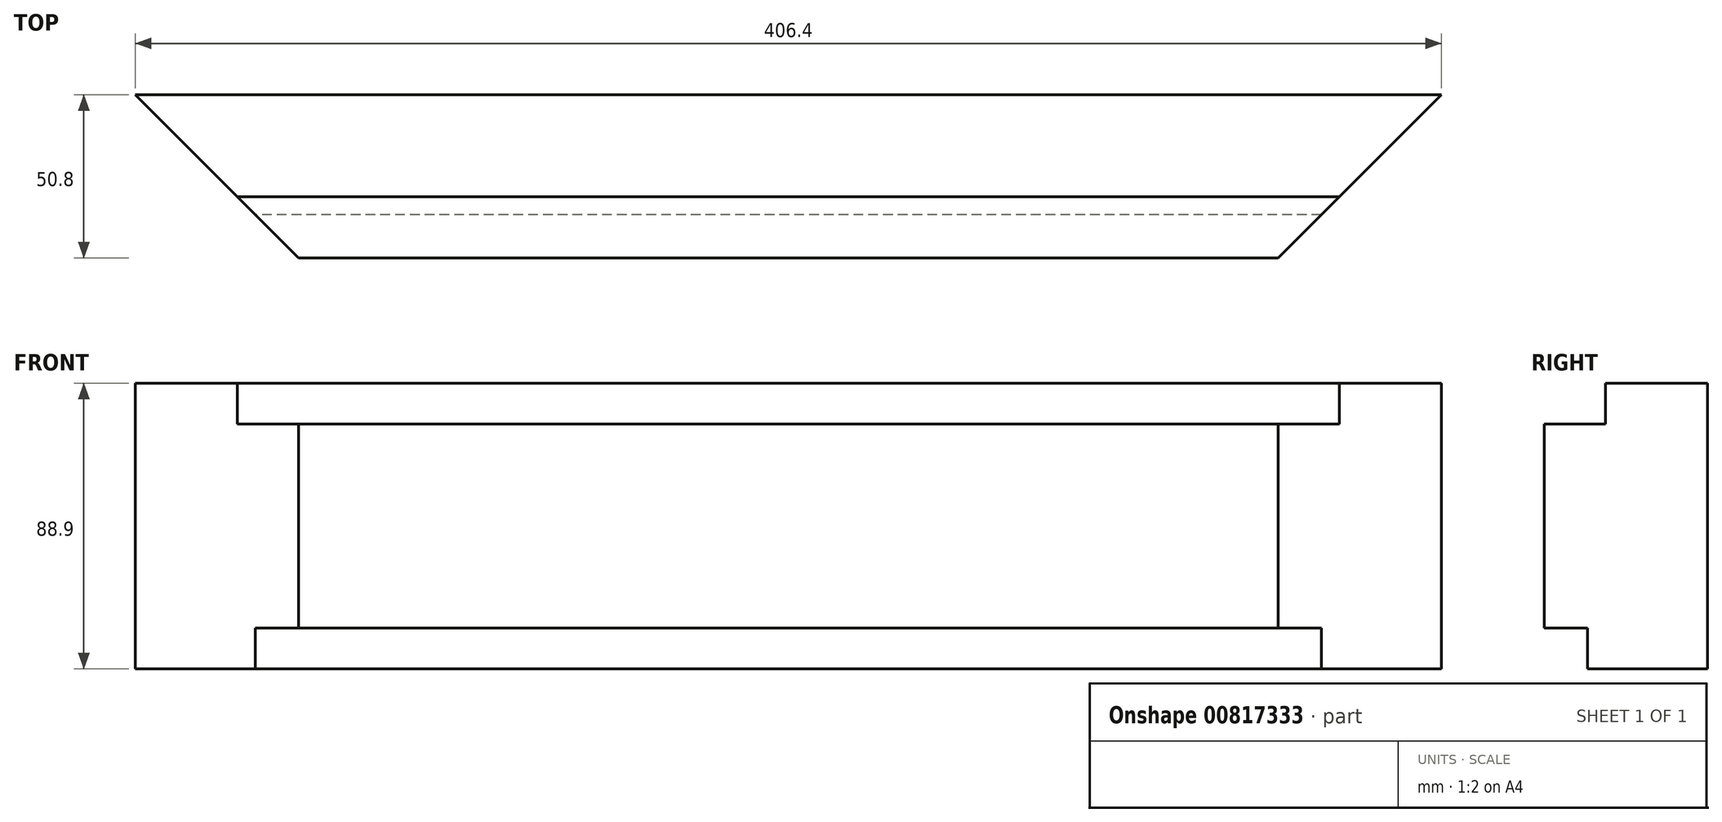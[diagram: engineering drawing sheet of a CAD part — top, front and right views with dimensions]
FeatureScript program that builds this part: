
annotation { "Feature Type Name" : "Feature", "Feature Type Description" : "" }
export const myFeature = defineFeature(function(context is Context, id is Id, definition is map)
    precondition{}
    {
        {
            var Q0;
            Q0=qCreatedBy(makeId("Top.planeOp"),FACE);
            var sketch = newSketch(context, id + "F0", { "sketchPlane" : qUnion([Q0])});
            skLineSegment(sketch, "E0.bottom", {"start": v(152.4, -25.4) * mm, "end": v(-152.4, -25.4) * mm});
            skLineSegment(sketch, "E0.top", {"start": v(152.4, 25.4) * mm, "end": v(-152.4, 25.4) * mm});
            skLineSegment(sketch, "E0.left", {"start": v(152.4, -25.4) * mm, "end": v(152.4, 25.4) * mm});
            skLineSegment(sketch, "E0.right", {"start": v(-152.4, -25.4) * mm, "end": v(-152.4, 25.4) * mm});
            skPoint(sketch, "E0.middle", {"position": v(0, 0) * mm});
            skSolve(sketch);
        }
        {
            var Q0;
            Q0=makeQuery(id+"F0.imprint","IMPRINT",FACE,{"disambiguationData":[TD([[makeQuery(id+"F0.imprint","IMPRINT",EDGE,{"derivedFrom":sQuery(id+"F0.wireOp",EDGE,"E0.bottom")}),-1.0]])]});
            extrude(context, id + "F1", {"entities" : qUnion([Q0]), "depth" : 88.9 * mm, "offsetDistance" : 25.4 * mm});
        }
        {
            var Q0;
            Q0=makeQuery(id+"F1.opExtrude","CAP_FACE",FACE,{"disambiguationData":[OSD([sQuery(id+"F0.wireOp",EDGE,"E0.bottom"),sQuery(id+"F0.wireOp",EDGE,"E0.top"),sQuery(id+"F0.wireOp",EDGE,"E0.left"),sQuery(id+"F0.wireOp",EDGE,"E0.right")])],"isStart":false});
            var sketch = newSketch(context, id + "F2", { "sketchPlane" : qUnion([Q0])});
            skLineSegment(sketch, "E1", {"start": v(-152.4, -6.35) * mm, "end": v(152.4, -6.35) * mm});
            skSolve(sketch);
        }
        {
            var Q0;
            {var subQ0=sQuery(id+"F2.wireOp",EDGE,"E1");Q0=makeQuery(id+"F2.imprint","IMPRINT",FACE,{"disambiguationData":[TD([[makeQuery(id+"F2.imprint","IMPRINT",EDGE,{"derivedFrom":subQ0}),-1.0]])]});}
            extrude(context, id + "F3", {"entities" : qUnion([Q0]), "operationType" : NewBodyOperationType.REMOVE, "oppositeDirection" : true, "depth" : 12.7 * mm, "offsetDistance" : 25.4 * mm});
        }
        {
            var Q0;
            Q0=qCreatedBy(makeId("Top.planeOp"),FACE);
            var sketch = newSketch(context, id + "F4", { "sketchPlane" : qUnion([Q0])});
            skLineSegment(sketch, "E2", {"start": v(152.4, -25.4) * mm, "end": v(152.4, 25.4) * mm});
            skLineSegment(sketch, "E3", {"start": v(152.4, 25.4) * mm, "end": v(203.2, 25.4) * mm});
            skLineSegment(sketch, "E4", {"start": v(203.2, 25.4) * mm, "end": v(152.4, -25.4) * mm});
            skSolve(sketch);
        }
        {
            var Q0;
            Q0=makeQuery(id+"F4.imprint","IMPRINT",FACE,{"disambiguationData":[TD([[makeQuery(id+"F4.imprint","IMPRINT",EDGE,{"derivedFrom":sQuery(id+"F4.wireOp",EDGE,"E2")}),-1.0]])]});
            extrude(context, id + "F5", {"entities" : qUnion([Q0]), "operationType" : NewBodyOperationType.ADD, "depth" : 88.9 * mm, "offsetDistance" : 25.4 * mm});
        }
        {
            var Q0;
            Q0=makeQuery(id+"F5.boolean.opBoolean","MERGE",FACE,{"derivedFrom":[makeQuery(id+"F1.opExtrude","CAP_FACE",FACE,{"disambiguationData":[OSD([sQuery(id+"F0.wireOp",EDGE,"E0.bottom"),sQuery(id+"F0.wireOp",EDGE,"E0.top"),sQuery(id+"F0.wireOp",EDGE,"E0.left"),sQuery(id+"F0.wireOp",EDGE,"E0.right")])],"isStart":false}),makeQuery(id+"F5.opExtrude","CAP_FACE",FACE,{"disambiguationData":[OSD([sQuery(id+"F4.wireOp",EDGE,"E2"),sQuery(id+"F4.wireOp",EDGE,"E3"),sQuery(id+"F4.wireOp",EDGE,"E4")])],"isStart":false})]});
            var sketch = newSketch(context, id + "F6", { "sketchPlane" : qUnion([Q0])});
            skLineSegment(sketch, "E5", {"start": v(152.4, -6.35) * mm, "end": v(171.45, -6.35) * mm});
            skLineSegment(sketch, "E6", {"start": v(171.45, -6.35) * mm, "end": v(152.4, -25.4) * mm});
            skSolve(sketch);
        }
        {
            var Q0;
            Q0=makeQuery(id+"F6.imprint","IMPRINT",FACE,{"disambiguationData":[TD([[makeQuery(id+"F6.imprint","IMPRINT",EDGE,{"derivedFrom":sQuery(id+"F6.wireOp",EDGE,"E5")}),-1.0]])]});
            extrude(context, id + "F7", {"entities" : qUnion([Q0]), "operationType" : NewBodyOperationType.REMOVE, "oppositeDirection" : true, "depth" : 12.7 * mm, "offsetDistance" : 25.4 * mm});
        }
        {
            var Q0;
            Q0=qCreatedBy(makeId("Top.planeOp"),FACE);
            var sketch = newSketch(context, id + "F8", { "sketchPlane" : qUnion([Q0])});
            skLineSegment(sketch, "E7", {"start": v(-152.4, -25.4) * mm, "end": v(-152.4, 25.4) * mm});
            skLineSegment(sketch, "E8", {"start": v(-152.4, 25.4) * mm, "end": v(-203.2, 25.4) * mm});
            skLineSegment(sketch, "E9", {"start": v(-203.2, 25.4) * mm, "end": v(-152.4, -25.4) * mm});
            skSolve(sketch);
        }
        {
            var Q0;
            Q0=makeQuery(id+"F8.imprint","IMPRINT",FACE,{"disambiguationData":[TD([[makeQuery(id+"F8.imprint","IMPRINT",EDGE,{"derivedFrom":sQuery(id+"F8.wireOp",EDGE,"E7")}),1.0]])]});
            extrude(context, id + "F9", {"entities" : qUnion([Q0]), "operationType" : NewBodyOperationType.ADD, "depth" : 88.9 * mm, "offsetDistance" : 25.4 * mm});
        }
        {
            var Q0;
            Q0=makeQuery(id+"F9.boolean.opBoolean","MERGE",FACE,{"derivedFrom":[makeQuery(id+"F5.boolean.opBoolean","MERGE",FACE,{"derivedFrom":[makeQuery(id+"F1.opExtrude","CAP_FACE",FACE,{"disambiguationData":[OSD([sQuery(id+"F0.wireOp",EDGE,"E0.bottom"),sQuery(id+"F0.wireOp",EDGE,"E0.top"),sQuery(id+"F0.wireOp",EDGE,"E0.left"),sQuery(id+"F0.wireOp",EDGE,"E0.right")])],"isStart":false}),makeQuery(id+"F5.opExtrude","CAP_FACE",FACE,{"disambiguationData":[OSD([sQuery(id+"F4.wireOp",EDGE,"E2"),sQuery(id+"F4.wireOp",EDGE,"E3"),sQuery(id+"F4.wireOp",EDGE,"E4")])],"isStart":false})]}),makeQuery(id+"F9.opExtrude","CAP_FACE",FACE,{"disambiguationData":[OSD([sQuery(id+"F8.wireOp",EDGE,"E7"),sQuery(id+"F8.wireOp",EDGE,"E8"),sQuery(id+"F8.wireOp",EDGE,"E9")])],"isStart":false})]});
            var sketch = newSketch(context, id + "F10", { "sketchPlane" : qUnion([Q0])});
            skLineSegment(sketch, "E10", {"start": v(-152.4, -25.4) * mm, "end": v(-152.4, -6.35) * mm});
            skLineSegment(sketch, "E11", {"start": v(-152.4, -6.35) * mm, "end": v(-171.45, -6.35) * mm});
            skLineSegment(sketch, "E12", {"start": v(-171.45, -6.35) * mm, "end": v(-152.4, -25.4) * mm});
            skSolve(sketch);
        }
        {
            var Q0;
            Q0=makeQuery(id+"F10.imprint","IMPRINT",FACE,{"disambiguationData":[TD([[makeQuery(id+"F10.imprint","IMPRINT",EDGE,{"derivedFrom":sQuery(id+"F10.wireOp",EDGE,"E10")}),1.0]])]});
            extrude(context, id + "F11", {"entities" : qUnion([Q0]), "operationType" : NewBodyOperationType.REMOVE, "oppositeDirection" : true, "depth" : 12.7 * mm, "offsetDistance" : 25.4 * mm});
        }
        {
            var Q0;
            Q0=makeQuery(id+"F9.boolean.opBoolean","MERGE",FACE,{"derivedFrom":[makeQuery(id+"F5.boolean.opBoolean","MERGE",FACE,{"derivedFrom":[makeQuery(id+"F1.opExtrude","CAP_FACE",FACE,{"disambiguationData":[OSD([sQuery(id+"F0.wireOp",EDGE,"E0.bottom"),sQuery(id+"F0.wireOp",EDGE,"E0.top"),sQuery(id+"F0.wireOp",EDGE,"E0.left"),sQuery(id+"F0.wireOp",EDGE,"E0.right")])],"isStart":true}),makeQuery(id+"F5.opExtrude","CAP_FACE",FACE,{"disambiguationData":[OSD([sQuery(id+"F4.wireOp",EDGE,"E2"),sQuery(id+"F4.wireOp",EDGE,"E3"),sQuery(id+"F4.wireOp",EDGE,"E4")])],"isStart":true})]}),makeQuery(id+"F9.opExtrude","CAP_FACE",FACE,{"disambiguationData":[OSD([sQuery(id+"F8.wireOp",EDGE,"E7"),sQuery(id+"F8.wireOp",EDGE,"E8"),sQuery(id+"F8.wireOp",EDGE,"E9")])],"isStart":true})]});
            var sketch = newSketch(context, id + "F12", { "sketchPlane" : qUnion([Q0])});
            skLineSegment(sketch, "E13", {"start": v(165.87, 11.93) * mm, "end": v(-165.87, 11.93) * mm});
            skSolve(sketch);
        }
        {
            var Q0;
            {var subQ0=sQuery(id+"F12.wireOp",EDGE,"E13");Q0=makeQuery(id+"F12.imprint","IMPRINT",FACE,{"disambiguationData":[TD([[makeQuery(id+"F12.imprint","IMPRINT",EDGE,{"derivedFrom":subQ0}),-1.0]])]});}
            extrude(context, id + "F13", {"entities" : qUnion([Q0]), "operationType" : NewBodyOperationType.REMOVE, "oppositeDirection" : true, "depth" : 12.7 * mm, "offsetDistance" : 25.4 * mm});
        }
    });
